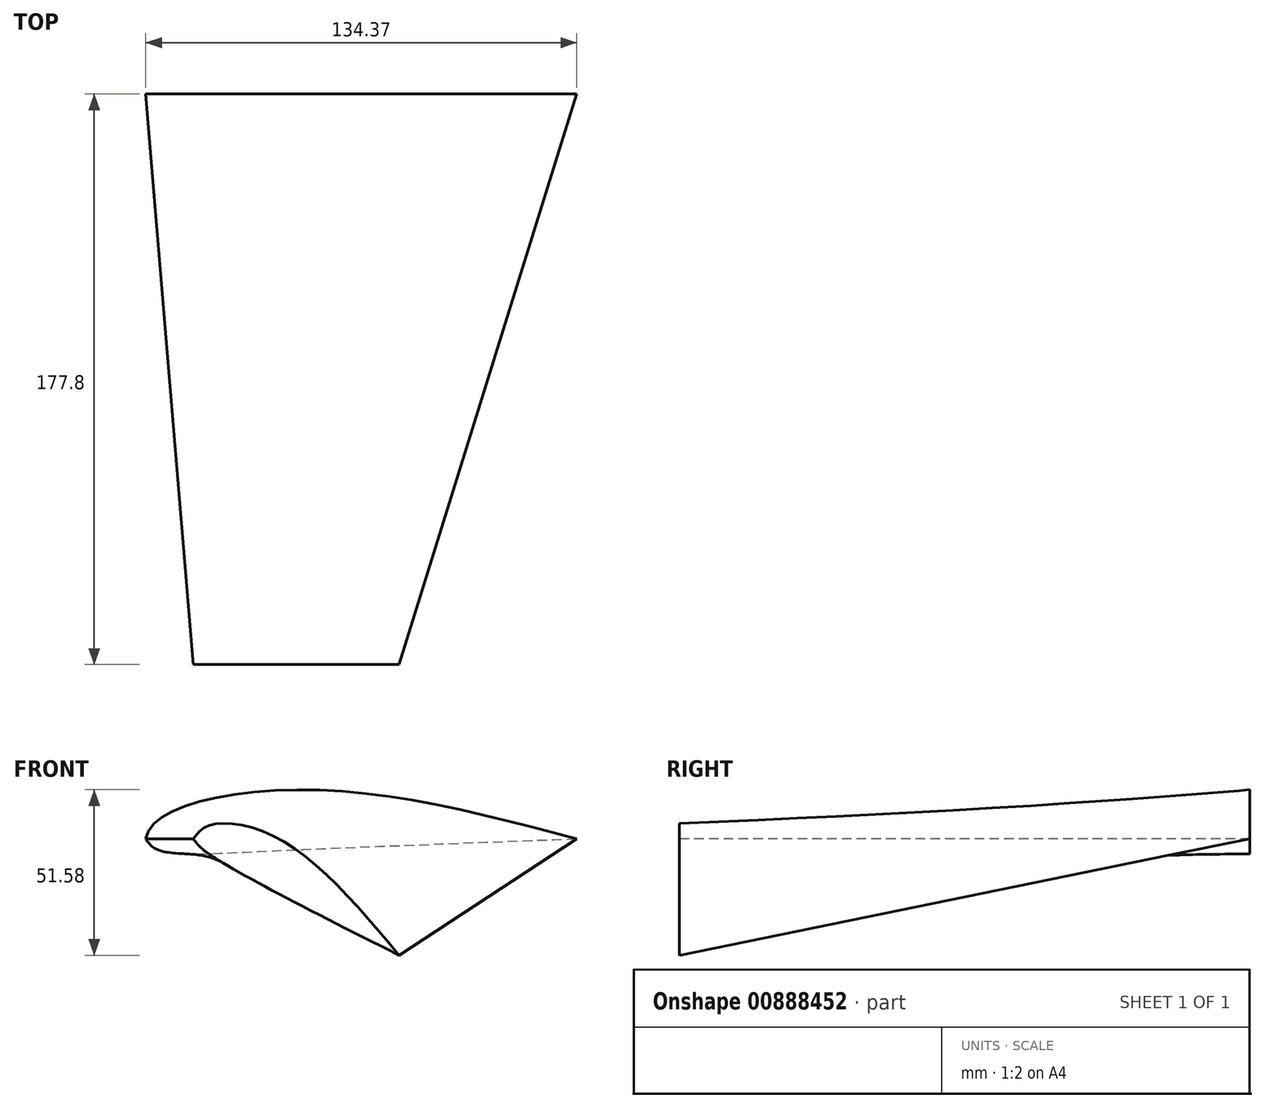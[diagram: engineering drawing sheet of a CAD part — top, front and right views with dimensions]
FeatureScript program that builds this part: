
annotation { "Feature Type Name" : "Feature", "Feature Type Description" : "" }
export const myFeature = defineFeature(function(context is Context, id is Id, definition is map)
    precondition{}
    {
        {
            var Q0;
            Q0=qCreatedBy(makeId("Front.planeOp"),FACE);
            var sketch = newSketch(context, id + "F0", { "sketchPlane" : qUnion([Q0])});
            skFitSpline(sketch, "E0", {"points": [v(-58.24, 0) * mm, v(-49.12, 8.95) * mm, v(0, 15.02) * mm, v(76.13, 0) * mm], "startDerivative": vector(9.77, 58.31) * mm, "endDerivative": vector(162.67, -43.21) * mm});
            skFitSpline(sketch, "E1", {"points": [v(-58.24, 0) * mm, v(-55.53, -2.87) * mm, v(-48.1, -4.56) * mm, v(-21.44, -3.88) * mm, v(76.13, 0) * mm], "startDerivative": vector(22.45, -31.7) * mm, "endDerivative": vector(223, 8.4) * mm});
            skSolve(sketch);
        }
        {
            var Q0;
            Q0=qCreatedBy(makeId("Front.planeOp"),FACE);
            cPlane(context, id + "F1", {"entities" : qUnion([Q0]), "cplaneType" : CPlaneType.OFFSET, "offset" : 177.8 * mm, "width" : 152.4 * mm, "height" : 152.4 * mm});
        }
        {
            var Q0;
            Q0=qCreatedBy(id+"F1.planeOp",FACE);
            var sketch = newSketch(context, id + "F2", { "sketchPlane" : qUnion([Q0])});
            skFitSpline(sketch, "E2", {"points": [v(-43.38, 0) * mm, v(-38.32, 4.22) * mm, v(-16.71, 0) * mm, v(20.76, -36.3) * mm], "startDerivative": vector(21.68, 28.54) * mm, "endDerivative": vector(73.88, -88.25) * mm});
            skFitSpline(sketch, "E3", {"points": [v(-43.38, 0) * mm, v(-39.67, -3.88) * mm, v(20.76, -36.3) * mm], "startDerivative": vector(10.38, -15.16) * mm, "endDerivative": vector(100.93, -50.75) * mm});
            skSolve(sketch);
        }
        {
            var Q0;
            Q0=makeQuery(id+"F0.imprint","IMPRINT",FACE,{"disambiguationData":[TD([[makeQuery(id+"F0.imprint","IMPRINT",EDGE,{"derivedFrom":sQuery(id+"F0.wireOp",EDGE,"E0")}),-1.0]])]});
            var Q1;
            Q1=makeQuery(id+"F2.imprint","IMPRINT",FACE,{"disambiguationData":[TD([[makeQuery(id+"F2.imprint","IMPRINT",EDGE,{"derivedFrom":sQuery(id+"F2.wireOp",EDGE,"E2")}),-1.0]])]});
            loft(context, id + "F3", {"sheetProfilesArray" : [{ "sheetProfileEntities" : qUnion([Q0]) }, { "sheetProfileEntities" : qUnion([Q1]) }]});
        }
    });
